# Revit family: Building-IEC309Boards-GEWISS-68QDIN-DISTRIBUTION-BOARD-10MOD_5SOCKET-OUTLETS
name_source: partatom
category: Apparecchi elettrici
units: mm (PartAtom-declared; Revit-internal decimal feet)

## family parameters
Condiviso = No
Host = Superficie
Mantenere orientamento annotazione = Sì
Punto di calcolo locali = Sì
Quota connettore circolare = Usa diametro
Taglio con vuoti quando caricato = No
Tipo di parte = Normale

## types (1)
- GW68027N - Q-DIN 10M 3S.O.50X50 2S.O.16/32A IP65
    Accordance with Standards = EN 62208
    Catalogue = BUILDING
    Colour = Grey RAL 7035
    Descrizione = Q-DIN 10M 3S.O.50X50 2S.O.16/32A IP65
    Dispersible power A (W) = 16
    Dispersible power B (W) = 42
    Electrocod = 2242
    Glow Wire Test = 650°C
    Houseable socket = 3 dom.socket 50x50 mm + 2 IEC 16/32 A
    IDF = d8e117f9-8f25-4e2f-aa71-76ea3311fd0d
    IDT = e98e3194ef624e34ab5d6b273797aa67
    IP degree = IP65
    Immagine tipo = GW68027N.jpg
    Installation type = Surface-mounting
    Insulation class = II
    Modello = GW68027N
    No. of modules EN 50022 = 10
    No. of provided blank lids = 1 domestic + 1 IEC 16 A
    POMELLO = bianco
    PRESA = rosso
    Produttore = GEWISS S.p.A.
    Prospetto di default = 1219 mm
    SEO = Board
    STRUTTURA = RAL - 7035
    STRUTTURA ALTA = Poche
    Shock resistance = IK08
    Spostamento_S = 1000 mm  [stored 3.28084 ft]
    Technical sheet = https://www.gewiss.com
    Thermo-pressure with ball = 70
    URL = https://www.gewiss.com
    VETRO = Vetro
    Version file RFA = 21.5
    Version type = Empty

note: source unit labels omitted for Thermo-pressure with ball — the stored unit's dimension contradicts the parameter name (converter mislabeling)

note: [stored X ft] marks values corroborated as IEEE doubles in the binary element streams (Revit-internal decimal feet)

## geometry (parser evidence)
native form markers: Sweep x5
no freeform markers — native parametric forms only
